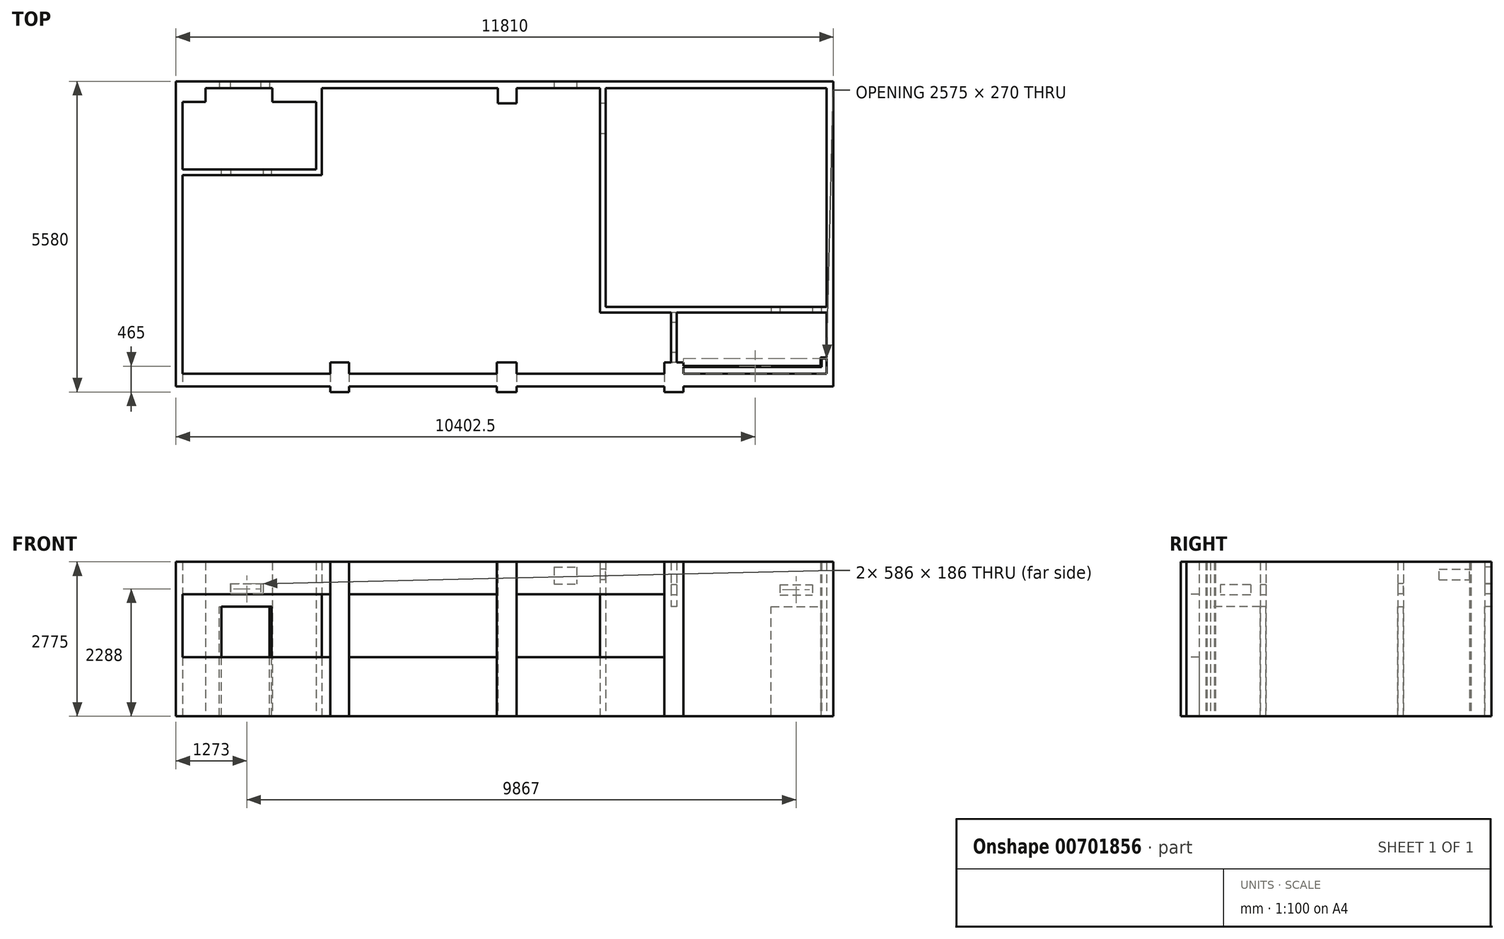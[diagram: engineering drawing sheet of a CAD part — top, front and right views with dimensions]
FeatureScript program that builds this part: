
annotation { "Feature Type Name" : "Feature", "Feature Type Description" : "" }
export const myFeature = defineFeature(function(context is Context, id is Id, definition is map)
    precondition{}
    {
        {
            var Q0;
            Q0=qCreatedBy(makeId("Top.planeOp"),FACE);
            var sketch = newSketch(context, id + "F0", { "sketchPlane" : qUnion([Q0])});
            skLineSegment(sketch, "E0.bottom", {"start": v(0, 0) * mm, "end": v(-5570, 0) * mm});
            skLineSegment(sketch, "E0.top", {"start": v(0, -5240) * mm, "end": v(-2575, -5240) * mm, "construction": true});
            skLineSegment(sketch, "E0.left", {"start": v(0, 0) * mm, "end": v(0, -5240) * mm});
            skLineSegment(sketch, "E0.right", {"start": v(-11570, -250) * mm, "end": v(-11570, -5130) * mm});
            skLineSegment(sketch, "E1.bottom", {"start": v(-11690, 120) * mm, "end": v(120, 120) * mm});
            skLineSegment(sketch, "E1.top", {"start": v(-11690, -5360) * mm, "end": v(-8920, -5360) * mm});
            skLineSegment(sketch, "E1.left", {"start": v(-11690, 120) * mm, "end": v(-11690, -5360) * mm});
            skLineSegment(sketch, "E1.right", {"start": v(120, 120) * mm, "end": v(120, -5360) * mm});
            skLineSegment(sketch, "E2.trimOffspring", {"start": v(-5925, -5240) * mm, "end": v(-8580, -5240) * mm, "construction": true});
            skLineSegment(sketch, "E3.trimOffspring", {"start": v(-5910, 0) * mm, "end": v(-9070, 0) * mm});
            skLineSegment(sketch, "E4", {"start": v(-5910, 0) * mm, "end": v(-5910, -275) * mm});
            skLineSegment(sketch, "E5", {"start": v(-5910, -275) * mm, "end": v(-5570, -275) * mm});
            skLineSegment(sketch, "E6", {"start": v(-5570, -275) * mm, "end": v(-5570, 0) * mm});
            skLineSegment(sketch, "E7", {"start": v(-5925, -5130) * mm, "end": v(-5925, -4930) * mm});
            skLineSegment(sketch, "E8", {"start": v(-5925, -4930) * mm, "end": v(-5570, -4930) * mm});
            skLineSegment(sketch, "E9", {"start": v(-5570, -4930) * mm, "end": v(-5570, -5130) * mm});
            skLineSegment(sketch, "E10.top", {"start": v(-8580, -4930) * mm, "end": v(-8920, -4930) * mm});
            skLineSegment(sketch, "E10.left", {"start": v(-8580, -5130) * mm, "end": v(-8580, -4930) * mm});
            skLineSegment(sketch, "E10.right", {"start": v(-8920, -5130) * mm, "end": v(-8920, -4930) * mm});
            skLineSegment(sketch, "E11.trimOffspring", {"start": v(-8920, -5240) * mm, "end": v(-11570, -5240) * mm, "construction": true});
            skLineSegment(sketch, "E12.top", {"start": v(-11570, -250) * mm, "end": v(-11160, -250) * mm});
            skLineSegment(sketch, "E12.right", {"start": v(-11160, 0) * mm, "end": v(-11160, -250) * mm});
            skLineSegment(sketch, "E13.top", {"start": v(-9960, -250) * mm, "end": v(-9070, -250) * mm});
            skLineSegment(sketch, "E13.left", {"start": v(-9960, 0) * mm, "end": v(-9960, -250) * mm});
            skLineSegment(sketch, "E13.right", {"start": v(-9070, 0) * mm, "end": v(-9070, -250) * mm});
            skLineSegment(sketch, "E14.trimOffspring", {"start": v(-9960, 0) * mm, "end": v(-11160, 0) * mm});
            skLineSegment(sketch, "E15.top", {"start": v(-2915, -4930) * mm, "end": v(-2575, -4930) * mm});
            skLineSegment(sketch, "E15.left", {"start": v(-2915, -5130) * mm, "end": v(-2915, -4930) * mm});
            skLineSegment(sketch, "E15.right", {"start": v(-2575, -5130) * mm, "end": v(-2575, -4930) * mm});
            skLineSegment(sketch, "E16.top", {"start": v(-2575, -5460) * mm, "end": v(-2915, -5460) * mm});
            skLineSegment(sketch, "E16.left", {"start": v(-2575, -5360) * mm, "end": v(-2575, -5460) * mm});
            skLineSegment(sketch, "E16.right", {"start": v(-2915, -5360) * mm, "end": v(-2915, -5460) * mm});
            skLineSegment(sketch, "E17.trimOffspring", {"start": v(-2575, -5360) * mm, "end": v(120, -5360) * mm});
            skLineSegment(sketch, "E18.trimOffspring", {"start": v(-2915, -5240) * mm, "end": v(-5570, -5240) * mm, "construction": true});
            skLineSegment(sketch, "E19.top", {"start": v(-5570, -5460) * mm, "end": v(-5925, -5460) * mm});
            skLineSegment(sketch, "E19.left", {"start": v(-5570, -5360) * mm, "end": v(-5570, -5460) * mm});
            skLineSegment(sketch, "E19.right", {"start": v(-5925, -5360) * mm, "end": v(-5925, -5460) * mm});
            skLineSegment(sketch, "E20.top", {"start": v(-8580, -5460) * mm, "end": v(-8920, -5460) * mm});
            skLineSegment(sketch, "E20.left", {"start": v(-8580, -5360) * mm, "end": v(-8580, -5460) * mm});
            skLineSegment(sketch, "E20.right", {"start": v(-8920, -5360) * mm, "end": v(-8920, -5460) * mm});
            skLineSegment(sketch, "E21.trimOffspring", {"start": v(-8580, -5360) * mm, "end": v(-5925, -5360) * mm});
            skLineSegment(sketch, "E22.trimOffspring", {"start": v(-5570, -5360) * mm, "end": v(-2915, -5360) * mm});
            skLineSegment(sketch, "E23", {"start": v(-11570, -5130) * mm, "end": v(-8920, -5130) * mm});
            skLineSegment(sketch, "E24.trimOffspring", {"start": v(-8580, -5130) * mm, "end": v(-5925, -5130) * mm});
            skLineSegment(sketch, "E25.trimOffspring", {"start": v(-5570, -5130) * mm, "end": v(-2915, -5130) * mm});
            skLineSegment(sketch, "E26.trimOffspring", {"start": v(-2575, -5130) * mm, "end": v(0, -5130) * mm});
            skSolve(sketch);
        }
        {
            var Q0;
            Q0=qSketchRegion(id+"F0",true);
            extrude(context, id + "F1", {"entities" : qUnion([Q0]), "depth" : 2775 * mm, "offsetDistance" : 25 * mm});
        }
        {
            var Q0;
            Q0=makeQuery(id+"F1.opExtrude","SWEPT_FACE",FACE,{"disambiguationData":[OSD([sQuery(id+"F0.wireOp",EDGE,"E0.bottom")])]});
            var sketch = newSketch(context, id + "F2", { "sketchPlane" : qUnion([Q0])});
            skLineSegment(sketch, "E27.bottom", {"start": v(-10910, 0) * mm, "end": v(-10010, 0) * mm});
            skLineSegment(sketch, "E27.top", {"start": v(-10910, 1970) * mm, "end": v(-10010, 1970) * mm});
            skLineSegment(sketch, "E27.left", {"start": v(-10910, 0) * mm, "end": v(-10910, 1970) * mm});
            skLineSegment(sketch, "E27.right", {"start": v(-10010, 0) * mm, "end": v(-10010, 1970) * mm});
            skSolve(sketch);
        }
        {
            var Q0;
            Q0=qSketchRegion(id+"F2",true);
            extrude(context, id + "F3", {"entities" : qUnion([Q0]), "operationType" : NewBodyOperationType.REMOVE, "endBound" : BoundingType.UP_TO_NEXT, "oppositeDirection" : true, "depth" : 25 * mm, "offsetDistance" : 25 * mm});
        }
        {
            var Q0;
            Q0=qCreatedBy(makeId("Top.planeOp"),FACE);
            var sketch = newSketch(context, id + "F4", { "sketchPlane" : qUnion([Q0])});
            skLineSegment(sketch, "E28.bottom", {"start": v(-9070, -1460) * mm, "end": v(-11570, -1460) * mm});
            skLineSegment(sketch, "E28.top", {"start": v(-9070, -1560) * mm, "end": v(-11570, -1560) * mm});
            skLineSegment(sketch, "E28.right", {"start": v(-11570, -1460) * mm, "end": v(-11570, -1560) * mm});
            skLineSegment(sketch, "E29", {"start": v(-9070, -1460) * mm, "end": v(-9070, -1560) * mm});
            skSolve(sketch);
        }
        {
            var Q0;
            Q0=makeQuery(id+"F4.imprint","IMPRINT",FACE,{"disambiguationData":[TD([[makeQuery(id+"F4.imprint","IMPRINT",EDGE,{"derivedFrom":sQuery(id+"F4.wireOp",EDGE,"E28.bottom")}),1.0]])]});
            var Q1;
            {var subQ0=sQuery(id+"F0.wireOp",EDGE,"E1.right");var subQ1=sQuery(id+"F0.wireOp",EDGE,"E1.left");var subQ2=sQuery(id+"F0.wireOp",EDGE,"E1.top");var subQ3=sQuery(id+"F0.wireOp",EDGE,"E1.bottom");var subQ4=sQuery(id+"F0.wireOp",EDGE,"E0.right");var subQ5=sQuery(id+"F0.wireOp",EDGE,"E0.left");var subQ6=sQuery(id+"F0.wireOp",EDGE,"E0.top");var subQ7=sQuery(id+"F0.wireOp",EDGE,"E0.bottom");Q1=makeQuery(id+"FWLc4urFRa7aNsW_1.boolean.opBoolean","MERGE",FACE,{"derivedFrom":[makeQuery(id+"F1.opExtrude","CAP_FACE",FACE,{"disambiguationData":[OSD([subQ7,subQ6,subQ5,subQ4,subQ3,subQ2,subQ1,subQ0])],"isStart":false}),makeQuery(id+"FWLc4urFRa7aNsW_1.opExtrude","CAP_FACE",FACE,{"disambiguationData":[OSD([subQ7,subQ6,subQ5,subQ4,subQ3,subQ2,subQ1,subQ0])],"isStart":false})]});}
            extrude(context, id + "F5", {"entities" : qUnion([Q0]), "operationType" : NewBodyOperationType.ADD, "endBound" : BoundingType.UP_TO_SURFACE, "depth" : 25 * mm, "endBoundEntityFace" : qUnion([Q1]), "offsetDistance" : 25 * mm});
        }
        {
            var Q0;
            Q0=qCreatedBy(makeId("Top.planeOp"),FACE);
            var sketch = newSketch(context, id + "F6", { "sketchPlane" : qUnion([Q0])});
            skLineSegment(sketch, "E30.bottom", {"start": v(-9070, 0) * mm, "end": v(-9170, 0) * mm});
            skLineSegment(sketch, "E30.top", {"start": v(-9070, -1460) * mm, "end": v(-9170, -1460) * mm});
            skLineSegment(sketch, "E30.left", {"start": v(-9070, 0) * mm, "end": v(-9070, -1460) * mm});
            skLineSegment(sketch, "E30.right", {"start": v(-9170, 0) * mm, "end": v(-9170, -1460) * mm});
            skSolve(sketch);
        }
        {
            var Q0;
            Q0=makeQuery(id+"F6.imprint","IMPRINT",FACE,{"disambiguationData":[TD([[makeQuery(id+"F6.imprint","IMPRINT",EDGE,{"derivedFrom":sQuery(id+"F6.wireOp",EDGE,"E30.bottom")}),1.0]])]});
            var Q1;
            {var subQ0=sQuery(id+"F0.wireOp",EDGE,"E1.right");var subQ1=sQuery(id+"F0.wireOp",EDGE,"E1.left");var subQ2=sQuery(id+"F0.wireOp",EDGE,"E1.top");var subQ3=sQuery(id+"F0.wireOp",EDGE,"E1.bottom");var subQ4=sQuery(id+"F0.wireOp",EDGE,"E0.right");var subQ5=sQuery(id+"F0.wireOp",EDGE,"E0.left");var subQ6=sQuery(id+"F0.wireOp",EDGE,"E0.top");var subQ7=sQuery(id+"F0.wireOp",EDGE,"E0.bottom");Q1=makeQuery(id+"F5.boolean.opBoolean","MERGE",FACE,{"derivedFrom":[makeQuery(id+"FWLc4urFRa7aNsW_1.boolean.opBoolean","MERGE",FACE,{"derivedFrom":[makeQuery(id+"F1.opExtrude","CAP_FACE",FACE,{"disambiguationData":[OSD([subQ7,subQ6,subQ5,subQ4,subQ3,subQ2,subQ1,subQ0])],"isStart":false}),makeQuery(id+"FWLc4urFRa7aNsW_1.opExtrude","CAP_FACE",FACE,{"disambiguationData":[OSD([subQ7,subQ6,subQ5,subQ4,subQ3,subQ2,subQ1,subQ0])],"isStart":false})]}),makeQuery(id+"F5.opExtrude","CAP_FACE",FACE,{"disambiguationData":[OSD([subQ7,subQ6,subQ5,subQ4,subQ3,subQ2,subQ1,subQ0])],"isStart":false})]});}
            extrude(context, id + "F7", {"entities" : qUnion([Q0]), "operationType" : NewBodyOperationType.ADD, "endBound" : BoundingType.UP_TO_SURFACE, "depth" : 25 * mm, "endBoundEntityFace" : qUnion([Q1]), "offsetDistance" : 25 * mm});
        }
        {
            var Q0;
            {var subQ0=sQuery(id+"F0.wireOp",EDGE,"E0.right");var subQ8=sQuery(id+"F4.wireOp",EDGE,"E28.bottom");Q0=makeQuery(id+"F7.boolean.opBoolean","SPLIT",FACE,{"disambiguationData":[TD([makeQuery(id+"F1.opExtrude","SWEPT_FACE",FACE,{"disambiguationData":[OSD([subQ0])]})])],"derivedFrom":makeQuery(id+"F5.opExtrude","SWEPT_FACE",FACE,{"disambiguationData":[OSD([subQ8])]})});}
            var sketch = newSketch(context, id + "F8", { "sketchPlane" : qUnion([Q0])});
            skLineSegment(sketch, "E31.bottom", {"start": v(9970, 0) * mm, "end": v(10870, 0) * mm});
            skLineSegment(sketch, "E31.top", {"start": v(9970, 1970) * mm, "end": v(10870, 1970) * mm});
            skLineSegment(sketch, "E31.left", {"start": v(9970, 0) * mm, "end": v(9970, 1970) * mm});
            skLineSegment(sketch, "E31.right", {"start": v(10870, 0) * mm, "end": v(10870, 1970) * mm});
            skSolve(sketch);
        }
        {
            var Q0;
            Q0=makeQuery(id+"F8.imprint","IMPRINT",FACE,{"disambiguationData":[TD([[makeQuery(id+"F8.imprint","IMPRINT",EDGE,{"derivedFrom":sQuery(id+"F8.wireOp",EDGE,"E31.bottom")}),1.0]])]});
            extrude(context, id + "F9", {"entities" : qUnion([Q0]), "operationType" : NewBodyOperationType.REMOVE, "endBound" : BoundingType.UP_TO_NEXT, "oppositeDirection" : true, "depth" : 25 * mm, "offsetDistance" : 25 * mm});
        }
        {
            var Q0;
            Q0=qCreatedBy(makeId("Top.planeOp"),FACE);
            var sketch = newSketch(context, id + "F10", { "sketchPlane" : qUnion([Q0])});
            skLineSegment(sketch, "E32", {"start": v(-3970, -3930) * mm, "end": v(0, -3930) * mm});
            skLineSegment(sketch, "E33", {"start": v(-3970, -3930) * mm, "end": v(-3970, 0) * mm});
            skLineSegment(sketch, "E34", {"start": v(-3970, 0) * mm, "end": v(-4070, 0) * mm});
            skLineSegment(sketch, "E35", {"start": v(-4070, 0) * mm, "end": v(-4070, -4030) * mm});
            skLineSegment(sketch, "E36", {"start": v(-2795, -4030) * mm, "end": v(-4070, -4030) * mm});
            skLineSegment(sketch, "E37", {"start": v(0, -3930) * mm, "end": v(0, -4030) * mm});
            skLineSegment(sketch, "E38.top", {"start": v(-2795, -4930) * mm, "end": v(-2695, -4930) * mm});
            skLineSegment(sketch, "E38.left", {"start": v(-2795, -4030) * mm, "end": v(-2795, -4930) * mm});
            skLineSegment(sketch, "E38.right", {"start": v(-2695, -4030) * mm, "end": v(-2695, -4930) * mm});
            skPoint(sketch, "E39", {"position": v(-2745, -4930) * mm});
            skLineSegment(sketch, "E40.trimOffspring", {"start": v(0, -4030) * mm, "end": v(-2695, -4030) * mm});
            skSolve(sketch);
        }
        {
            var Q0;
            Q0=makeQuery(id+"F10.imprint","IMPRINT",FACE,{"disambiguationData":[TD([[makeQuery(id+"F10.imprint","IMPRINT",EDGE,{"derivedFrom":sQuery(id+"F10.wireOp",EDGE,"E32")}),-1.0]])]});
            extrude(context, id + "F11", {"entities" : qUnion([Q0]), "operationType" : NewBodyOperationType.ADD, "depth" : 2775 * mm, "offsetDistance" : 25 * mm});
        }
        {
            var Q0;
            Q0=makeQuery(id+"F1.opExtrude","SWEPT_FACE",FACE,{"disambiguationData":[OSD([sQuery(id+"F0.wireOp",EDGE,"E1.top")])]});
            var sketch = newSketch(context, id + "F12", { "sketchPlane" : qUnion([Q0])});
            skLineSegment(sketch, "E41.bottom", {"start": v(-2915, 2190) * mm, "end": v(-5570, 2190) * mm});
            skLineSegment(sketch, "E41.top", {"start": v(-2915, 1060) * mm, "end": v(-5570, 1060) * mm});
            skLineSegment(sketch, "E41.left", {"start": v(-2915, 2190) * mm, "end": v(-2915, 1060) * mm});
            skLineSegment(sketch, "E41.right", {"start": v(-5570, 2190) * mm, "end": v(-5570, 1060) * mm});
            skSolve(sketch);
        }
        {
            var Q0;
            Q0=makeQuery(id+"F12.imprint","IMPRINT",FACE,{"disambiguationData":[TD([[makeQuery(id+"F12.imprint","IMPRINT",EDGE,{"derivedFrom":sQuery(id+"F12.wireOp",EDGE,"UQFrSV9A-AeNk-hTGs-XUq7-kkI5QUDZIYbv.bottom")}),1.0]])]});
            var Q1;
            Q1=makeQuery(id+"F12.imprint","IMPRINT",FACE,{"disambiguationData":[TD([[makeQuery(id+"F12.imprint","IMPRINT",EDGE,{"derivedFrom":sQuery(id+"F12.wireOp",EDGE,"E41.bottom")}),1.0]])]});
            extrude(context, id + "F13", {"entities" : qUnion([Q0, Q1]), "operationType" : NewBodyOperationType.REMOVE, "endBound" : BoundingType.UP_TO_NEXT, "oppositeDirection" : true, "depth" : 25 * mm, "offsetDistance" : 25 * mm});
        }
        {
            var Q0;
            Q0=makeQuery(id+"F1.opExtrude","SWEPT_FACE",FACE,{"disambiguationData":[OSD([sQuery(id+"F0.wireOp",EDGE,"E1.top")])]});
            var sketch = newSketch(context, id + "F14", { "sketchPlane" : qUnion([Q0])});
            skLineSegment(sketch, "E42.bottom", {"start": v(-5925, 2190) * mm, "end": v(-8580, 2190) * mm});
            skLineSegment(sketch, "E42.top", {"start": v(-5925, 1060) * mm, "end": v(-8580, 1060) * mm});
            skLineSegment(sketch, "E42.left", {"start": v(-5925, 2190) * mm, "end": v(-5925, 1060) * mm});
            skLineSegment(sketch, "E42.right", {"start": v(-8580, 2190) * mm, "end": v(-8580, 1060) * mm});
            skLineSegment(sketch, "E43.bottom", {"start": v(-8920, 2190) * mm, "end": v(-11570, 2190) * mm});
            skLineSegment(sketch, "E43.top", {"start": v(-8920, 1060) * mm, "end": v(-11570, 1060) * mm});
            skLineSegment(sketch, "E43.left", {"start": v(-8920, 2190) * mm, "end": v(-8920, 1060) * mm});
            skLineSegment(sketch, "E43.right", {"start": v(-11570, 2190) * mm, "end": v(-11570, 1060) * mm});
            skSolve(sketch);
        }
        {
            var Q0;
            Q0=makeQuery(id+"F14.imprint","IMPRINT",FACE,{"disambiguationData":[TD([[makeQuery(id+"F14.imprint","IMPRINT",EDGE,{"derivedFrom":sQuery(id+"F14.wireOp",EDGE,"E43.bottom")}),1.0]])]});
            var Q1;
            Q1=makeQuery(id+"F14.imprint","IMPRINT",FACE,{"disambiguationData":[TD([[makeQuery(id+"F14.imprint","IMPRINT",EDGE,{"derivedFrom":sQuery(id+"F14.wireOp",EDGE,"E42.bottom")}),1.0]])]});
            extrude(context, id + "F15", {"entities" : qUnion([Q0, Q1]), "operationType" : NewBodyOperationType.REMOVE, "endBound" : BoundingType.UP_TO_NEXT, "oppositeDirection" : true, "depth" : 25 * mm, "offsetDistance" : 25 * mm});
        }
        {
            var Q0;
            Q0=makeQuery(id+"F1.opExtrude","SWEPT_FACE",FACE,{"disambiguationData":[OSD([sQuery(id+"F0.wireOp",EDGE,"E3.trimOffspring")])]});
            var sketch = newSketch(context, id + "F16", { "sketchPlane" : qUnion([Q0])});
            skLineSegment(sketch, "E44.bottom", {"start": v(-4896, 2680) * mm, "end": v(-4490, 2680) * mm});
            skLineSegment(sketch, "E44.top", {"start": v(-4896, 2374) * mm, "end": v(-4490, 2374) * mm});
            skLineSegment(sketch, "E44.left", {"start": v(-4896, 2680) * mm, "end": v(-4896, 2374) * mm});
            skLineSegment(sketch, "E44.right", {"start": v(-4490, 2680) * mm, "end": v(-4490, 2374) * mm});
            skSolve(sketch);
        }
        {
            var Q0;
            Q0=makeQuery(id+"F16.imprint","IMPRINT",FACE,{"disambiguationData":[TD([[makeQuery(id+"F16.imprint","IMPRINT",EDGE,{"derivedFrom":sQuery(id+"F16.wireOp",EDGE,"E44.bottom")}),-1.0]])]});
            extrude(context, id + "F17", {"entities" : qUnion([Q0]), "operationType" : NewBodyOperationType.REMOVE, "endBound" : BoundingType.UP_TO_NEXT, "oppositeDirection" : true, "depth" : 25 * mm, "offsetDistance" : 25 * mm});
        }
        {
            var Q0;
            Q0=makeQuery(id+"F11.opExtrude","SWEPT_FACE",FACE,{"disambiguationData":[OSD([sQuery(id+"F10.wireOp",EDGE,"E35")])]});
            var sketch = newSketch(context, id + "F18", { "sketchPlane" : qUnion([Q0])});
            skLineSegment(sketch, "E45.bottom", {"start": v(275, 2640) * mm, "end": v(821, 2640) * mm});
            skLineSegment(sketch, "E45.top", {"start": v(275, 2454) * mm, "end": v(821, 2454) * mm});
            skLineSegment(sketch, "E45.left", {"start": v(275, 2640) * mm, "end": v(275, 2454) * mm});
            skLineSegment(sketch, "E45.right", {"start": v(821, 2640) * mm, "end": v(821, 2454) * mm});
            skSolve(sketch);
        }
        {
            var Q0;
            Q0=makeQuery(id+"F18.imprint","IMPRINT",FACE,{"disambiguationData":[TD([[makeQuery(id+"F18.imprint","IMPRINT",EDGE,{"derivedFrom":sQuery(id+"F18.wireOp",EDGE,"E45.bottom")}),-1.0]])]});
            extrude(context, id + "F19", {"entities" : qUnion([Q0]), "operationType" : NewBodyOperationType.REMOVE, "endBound" : BoundingType.UP_TO_NEXT, "oppositeDirection" : true, "depth" : 25 * mm, "offsetDistance" : 25 * mm});
        }
        {
            var Q0;
            Q0=makeQuery(id+"F1.opExtrude","SWEPT_FACE",FACE,{"disambiguationData":[OSD([sQuery(id+"F0.wireOp",EDGE,"E14.trimOffspring")])]});
            var sketch = newSketch(context, id + "F20", { "sketchPlane" : qUnion([Q0])});
            skLineSegment(sketch, "E46.bottom", {"start": v(-10716, 2381) * mm, "end": v(-10170, 2381) * mm});
            skLineSegment(sketch, "E46.top", {"start": v(-10716, 2195) * mm, "end": v(-10170, 2195) * mm});
            skLineSegment(sketch, "E46.left", {"start": v(-10716, 2381) * mm, "end": v(-10716, 2195) * mm});
            skLineSegment(sketch, "E46.right", {"start": v(-10170, 2381) * mm, "end": v(-10170, 2195) * mm});
            skSolve(sketch);
        }
        {
            var Q0;
            Q0=makeQuery(id+"F20.imprint","IMPRINT",FACE,{"disambiguationData":[TD([[makeQuery(id+"F20.imprint","IMPRINT",EDGE,{"derivedFrom":sQuery(id+"F20.wireOp",EDGE,"E46.bottom")}),-1.0]])]});
            extrude(context, id + "F21", {"entities" : qUnion([Q0]), "operationType" : NewBodyOperationType.REMOVE, "endBound" : BoundingType.UP_TO_NEXT, "oppositeDirection" : true, "depth" : 25 * mm, "offsetDistance" : 25 * mm});
        }
        {
            var Q0;
            Q0=makeQuery(id+"F5.opExtrude","SWEPT_FACE",FACE,{"disambiguationData":[OSD([sQuery(id+"F4.wireOp",EDGE,"E28.top")])]});
            var sketch = newSketch(context, id + "F22", { "sketchPlane" : qUnion([Q0])});
            skLineSegment(sketch, "E47.bottom", {"start": v(-10710, 2381) * mm, "end": v(-10124, 2381) * mm});
            skLineSegment(sketch, "E47.top", {"start": v(-10710, 2195) * mm, "end": v(-10124, 2195) * mm});
            skLineSegment(sketch, "E47.left", {"start": v(-10710, 2381) * mm, "end": v(-10710, 2195) * mm});
            skLineSegment(sketch, "E47.right", {"start": v(-10124, 2381) * mm, "end": v(-10124, 2195) * mm});
            skSolve(sketch);
        }
        {
            var Q0;
            Q0=makeQuery(id+"F22.imprint","IMPRINT",FACE,{"disambiguationData":[TD([[makeQuery(id+"F22.imprint","IMPRINT",EDGE,{"derivedFrom":sQuery(id+"F22.wireOp",EDGE,"E47.bottom")}),-1.0]])]});
            extrude(context, id + "F23", {"entities" : qUnion([Q0]), "operationType" : NewBodyOperationType.REMOVE, "endBound" : BoundingType.UP_TO_NEXT, "oppositeDirection" : true, "depth" : 25 * mm, "offsetDistance" : 25 * mm});
        }
        {
            var Q0;
            Q0=qCreatedBy(makeId("Top.planeOp"),FACE);
            var sketch = newSketch(context, id + "F24", { "sketchPlane" : qUnion([Q0])});
            skLineSegment(sketch, "E48.bottom", {"start": v(-2575, -4990) * mm, "end": v(-110, -4990) * mm});
            skLineSegment(sketch, "E48.top", {"start": v(-2575, -5010) * mm, "end": v(-90, -5010) * mm});
            skLineSegment(sketch, "E48.left", {"start": v(-2575, -4990) * mm, "end": v(-2575, -5010) * mm});
            skLineSegment(sketch, "E49.bottom", {"start": v(0, -4840) * mm, "end": v(-110, -4840) * mm});
            skLineSegment(sketch, "E49.left", {"start": v(0, -4840) * mm, "end": v(0, -4860) * mm});
            skLineSegment(sketch, "E49.right", {"start": v(-110, -4840) * mm, "end": v(-110, -4990) * mm});
            skLineSegment(sketch, "E50.0", {"start": v(-90, -4860) * mm, "end": v(-90, -5010) * mm});
            skLineSegment(sketch, "E50.1", {"start": v(0, -4860) * mm, "end": v(-90, -4860) * mm});
            skSolve(sketch);
        }
        {
            var Q0;
            Q0=makeQuery(id+"F24.imprint","IMPRINT",FACE,{"disambiguationData":[TD([[makeQuery(id+"F24.imprint","IMPRINT",EDGE,{"derivedFrom":sQuery(id+"F24.wireOp",EDGE,"E48.bottom")}),-1.0]])]});
            var Q1;
            {var subQ0=sQuery(id+"F0.wireOp",EDGE,"E26.trimOffspring");var subQ1=sQuery(id+"F0.wireOp",EDGE,"E25.trimOffspring");var subQ2=sQuery(id+"F0.wireOp",EDGE,"E24.trimOffspring");var subQ3=sQuery(id+"F0.wireOp",EDGE,"E23");var subQ4=sQuery(id+"F0.wireOp",EDGE,"E22.trimOffspring");var subQ5=sQuery(id+"F0.wireOp",EDGE,"E21.trimOffspring");var subQ6=sQuery(id+"F0.wireOp",EDGE,"E20.right");var subQ7=sQuery(id+"F0.wireOp",EDGE,"E20.left");var subQ8=sQuery(id+"F0.wireOp",EDGE,"E20.top");var subQ9=sQuery(id+"F0.wireOp",EDGE,"E19.right");var subQ10=sQuery(id+"F0.wireOp",EDGE,"E19.left");var subQ11=sQuery(id+"F0.wireOp",EDGE,"E19.top");var subQ12=sQuery(id+"F0.wireOp",EDGE,"E17.trimOffspring");var subQ13=sQuery(id+"F0.wireOp",EDGE,"E16.right");var subQ14=sQuery(id+"F0.wireOp",EDGE,"E16.left");var subQ15=sQuery(id+"F0.wireOp",EDGE,"E16.top");var subQ16=sQuery(id+"F0.wireOp",EDGE,"E15.right");var subQ17=sQuery(id+"F0.wireOp",EDGE,"E15.left");var subQ18=sQuery(id+"F0.wireOp",EDGE,"E15.top");var subQ19=sQuery(id+"F0.wireOp",EDGE,"E14.trimOffspring");var subQ20=sQuery(id+"F0.wireOp",EDGE,"E13.right");var subQ21=sQuery(id+"F0.wireOp",EDGE,"E13.left");var subQ22=sQuery(id+"F0.wireOp",EDGE,"E13.top");var subQ23=sQuery(id+"F0.wireOp",EDGE,"E12.right");var subQ24=sQuery(id+"F0.wireOp",EDGE,"E12.top");var subQ25=sQuery(id+"F0.wireOp",EDGE,"E10.right");var subQ26=sQuery(id+"F0.wireOp",EDGE,"E10.left");var subQ27=sQuery(id+"F0.wireOp",EDGE,"E10.top");var subQ28=sQuery(id+"F0.wireOp",EDGE,"E9");var subQ29=sQuery(id+"F0.wireOp",EDGE,"E8");var subQ30=sQuery(id+"F0.wireOp",EDGE,"E7");var subQ31=sQuery(id+"F0.wireOp",EDGE,"E6");var subQ32=sQuery(id+"F0.wireOp",EDGE,"E5");var subQ33=sQuery(id+"F0.wireOp",EDGE,"E4");var subQ34=sQuery(id+"F0.wireOp",EDGE,"E3.trimOffspring");var subQ35=sQuery(id+"F0.wireOp",EDGE,"E1.right");var subQ36=sQuery(id+"F0.wireOp",EDGE,"E1.left");var subQ37=sQuery(id+"F0.wireOp",EDGE,"E1.top");var subQ38=sQuery(id+"F0.wireOp",EDGE,"E1.bottom");var subQ39=sQuery(id+"F0.wireOp",EDGE,"E0.right");var subQ40=sQuery(id+"F0.wireOp",EDGE,"E0.left");var subQ41=sQuery(id+"F0.wireOp",EDGE,"E0.bottom");Q1=makeQuery(id+"F11.boolean.opBoolean","MERGE",FACE,{"derivedFrom":[makeQuery(id+"F8GBdiIUWhZT2El_1.boolean.opBoolean","MERGE",FACE,{"derivedFrom":[makeQuery(id+"F7.boolean.opBoolean","MERGE",FACE,{"derivedFrom":[makeQuery(id+"F5.boolean.opBoolean","MERGE",FACE,{"derivedFrom":[makeQuery(id+"FWLc4urFRa7aNsW_1.boolean.opBoolean","MERGE",FACE,{"derivedFrom":[makeQuery(id+"F1.opExtrude","CAP_FACE",FACE,{"disambiguationData":[OSD([subQ41,subQ40,subQ39,subQ38,subQ37,subQ36,subQ35,subQ34,subQ33,subQ32,subQ31,subQ30,subQ29,subQ28,subQ27,subQ26,subQ25,subQ24,subQ23,subQ22,subQ21,subQ20,subQ19,subQ18,subQ17,subQ16,subQ15,subQ14,subQ13,subQ12,subQ11,subQ10,subQ9,subQ8,subQ7,subQ6,subQ5,subQ4,subQ3,subQ2,subQ1,subQ0])],"isStart":false}),makeQuery(id+"FWLc4urFRa7aNsW_1.opExtrude","CAP_FACE",FACE,{"disambiguationData":[OSD([subQ41,subQ40,subQ39,subQ38,subQ37,subQ36,subQ35,subQ34,subQ33,subQ32,subQ31,subQ30,subQ29,subQ28,subQ27,subQ26,subQ25,subQ24,subQ23,subQ22,subQ21,subQ20,subQ19,subQ18,subQ17,subQ16,subQ15,subQ14,subQ13,subQ12,subQ11,subQ10,subQ9,subQ8,subQ7,subQ6,subQ5,subQ4,subQ3,subQ2,subQ1,subQ0])],"isStart":false})]}),makeQuery(id+"F5.opExtrude","CAP_FACE",FACE,{"disambiguationData":[OSD([subQ41,subQ40,subQ39,subQ38,subQ37,subQ36,subQ35,subQ34,subQ33,subQ32,subQ31,subQ30,subQ29,subQ28,subQ27,subQ26,subQ25,subQ24,subQ23,subQ22,subQ21,subQ20,subQ19,subQ18,subQ17,subQ16,subQ15,subQ14,subQ13,subQ12,subQ11,subQ10,subQ9,subQ8,subQ7,subQ6,subQ5,subQ4,subQ3,subQ2,subQ1,subQ0])],"isStart":false})]}),makeQuery(id+"F7.opExtrude","CAP_FACE",FACE,{"disambiguationData":[OSD([subQ41,subQ40,subQ39,subQ38,subQ37,subQ36,subQ35,subQ34,subQ33,subQ32,subQ31,subQ30,subQ29,subQ28,subQ27,subQ26,subQ25,subQ24,subQ23,subQ22,subQ21,subQ20,subQ19,subQ18,subQ17,subQ16,subQ15,subQ14,subQ13,subQ12,subQ11,subQ10,subQ9,subQ8,subQ7,subQ6,subQ5,subQ4,subQ3,subQ2,subQ1,subQ0])],"isStart":false})]}),makeQuery(id+"F8GBdiIUWhZT2El_1.opExtrude","CAP_FACE",FACE,{"disambiguationData":[OSD([subQ41,subQ40,subQ39,subQ38,subQ37,subQ36,subQ35,subQ34,subQ33,subQ32,subQ31,subQ30,subQ29,subQ28,subQ27,subQ26,subQ25,subQ24,subQ23,subQ22,subQ21,subQ20,subQ19,subQ18,subQ17,subQ16,subQ15,subQ14,subQ13,subQ12,subQ11,subQ10,subQ9,subQ8,subQ7,subQ6,subQ5,subQ4,subQ3,subQ2,subQ1,subQ0])],"isStart":false})]}),makeQuery(id+"F11.opExtrude","CAP_FACE",FACE,{"disambiguationData":[OSD([subQ41,subQ40,subQ39,subQ38,subQ37,subQ36,subQ35,subQ34,subQ33,subQ32,subQ31,subQ30,subQ29,subQ28,subQ27,subQ26,subQ25,subQ24,subQ23,subQ22,subQ21,subQ20,subQ19,subQ18,subQ17,subQ16,subQ15,subQ14,subQ13,subQ12,subQ11,subQ10,subQ9,subQ8,subQ7,subQ6,subQ5,subQ4,subQ3,subQ2,subQ1,subQ0])],"isStart":false})]});}
            extrude(context, id + "F25", {"entities" : qUnion([Q0]), "operationType" : NewBodyOperationType.ADD, "endBound" : BoundingType.UP_TO_SURFACE, "depth" : 25 * mm, "endBoundEntityFace" : qUnion([Q1]), "offsetDistance" : 25 * mm});
        }
        {
            var Q0;
            Q0=makeQuery(id+"F11.opExtrude","SWEPT_FACE",FACE,{"disambiguationData":[OSD([sQuery(id+"F10.wireOp",EDGE,"E38.left")])]});
            var sketch = newSketch(context, id + "F26", { "sketchPlane" : qUnion([Q0])});
            skLineSegment(sketch, "E51.bottom", {"start": v(4030, 0) * mm, "end": v(4930, 0) * mm});
            skLineSegment(sketch, "E51.top", {"start": v(4030, 1970) * mm, "end": v(4930, 1970) * mm});
            skLineSegment(sketch, "E51.left", {"start": v(4030, 0) * mm, "end": v(4030, 1970) * mm});
            skLineSegment(sketch, "E51.right", {"start": v(4930, 0) * mm, "end": v(4930, 1970) * mm});
            skSolve(sketch);
        }
        {
            var Q0;
            Q0=makeQuery(id+"F26.imprint","IMPRINT",FACE,{"disambiguationData":[TD([[makeQuery(id+"F26.imprint","IMPRINT",EDGE,{"derivedFrom":sQuery(id+"F26.wireOp",EDGE,"E51.bottom")}),1.0]])]});
            extrude(context, id + "F27", {"entities" : qUnion([Q0]), "operationType" : NewBodyOperationType.REMOVE, "endBound" : BoundingType.UP_TO_NEXT, "oppositeDirection" : true, "depth" : 25 * mm, "offsetDistance" : 25 * mm});
        }
        {
            var Q0;
            Q0=makeQuery(id+"F11.opExtrude","SWEPT_FACE",FACE,{"disambiguationData":[OSD([sQuery(id+"F10.wireOp",EDGE,"E38.left")])]});
            var sketch = newSketch(context, id + "F28", { "sketchPlane" : qUnion([Q0])});
            skLineSegment(sketch, "E52.bottom", {"start": v(4207, 2366) * mm, "end": v(4753, 2366) * mm});
            skLineSegment(sketch, "E52.top", {"start": v(4207, 2180) * mm, "end": v(4753, 2180) * mm});
            skLineSegment(sketch, "E52.left", {"start": v(4207, 2366) * mm, "end": v(4207, 2180) * mm});
            skLineSegment(sketch, "E52.right", {"start": v(4753, 2366) * mm, "end": v(4753, 2180) * mm});
            skPoint(sketch, "E53", {"position": v(4480, 2180) * mm});
            skSolve(sketch);
        }
        {
            var Q0;
            Q0=makeQuery(id+"F28.imprint","IMPRINT",FACE,{"disambiguationData":[TD([[makeQuery(id+"F28.imprint","IMPRINT",EDGE,{"derivedFrom":sQuery(id+"F28.wireOp",EDGE,"E52.bottom")}),-1.0]])]});
            extrude(context, id + "F29", {"entities" : qUnion([Q0]), "operationType" : NewBodyOperationType.REMOVE, "endBound" : BoundingType.UP_TO_NEXT, "oppositeDirection" : true, "depth" : 25 * mm, "offsetDistance" : 25 * mm});
        }
        {
            var Q0;
            Q0=makeQuery(id+"F27.boolean.opBoolean","MERGE",FACE,{"derivedFrom":[makeQuery(id+"F11.opExtrude","SWEPT_FACE",FACE,{"disambiguationData":[OSD([sQuery(id+"F10.wireOp",EDGE,"E36")])]}),makeQuery(id+"F11.opExtrude","SWEPT_FACE",FACE,{"disambiguationData":[OSD([sQuery(id+"F10.wireOp",EDGE,"E40.trimOffspring")])]}),makeQuery(id+"F27.opExtrude","SWEPT_FACE",FACE,{"disambiguationData":[OSD([sQuery(id+"F26.wireOp",EDGE,"E51.left")])]})]});
            var sketch = newSketch(context, id + "F30", { "sketchPlane" : qUnion([Q0])});
            skLineSegment(sketch, "E54.bottom", {"start": v(-1000, 0) * mm, "end": v(-100, 0) * mm});
            skLineSegment(sketch, "E54.top", {"start": v(-1000, 1970) * mm, "end": v(-100, 1970) * mm});
            skLineSegment(sketch, "E54.left", {"start": v(-1000, 0) * mm, "end": v(-1000, 1970) * mm});
            skLineSegment(sketch, "E54.right", {"start": v(-100, 0) * mm, "end": v(-100, 1970) * mm});
            skSolve(sketch);
        }
        {
            var Q0;
            Q0=makeQuery(id+"F30.imprint","IMPRINT",FACE,{"disambiguationData":[TD([[makeQuery(id+"F30.imprint","IMPRINT",EDGE,{"derivedFrom":sQuery(id+"F30.wireOp",EDGE,"E54.bottom")}),-1.0]])]});
            extrude(context, id + "F31", {"entities" : qUnion([Q0]), "operationType" : NewBodyOperationType.REMOVE, "endBound" : BoundingType.UP_TO_NEXT, "oppositeDirection" : true, "depth" : 25 * mm, "offsetDistance" : 25 * mm});
        }
        {
            var Q0;
            Q0=makeQuery(id+"F27.boolean.opBoolean","MERGE",FACE,{"derivedFrom":[makeQuery(id+"F11.opExtrude","SWEPT_FACE",FACE,{"disambiguationData":[OSD([sQuery(id+"F10.wireOp",EDGE,"E36")])]}),makeQuery(id+"F11.opExtrude","SWEPT_FACE",FACE,{"disambiguationData":[OSD([sQuery(id+"F10.wireOp",EDGE,"E40.trimOffspring")])]}),makeQuery(id+"F27.opExtrude","SWEPT_FACE",FACE,{"disambiguationData":[OSD([sQuery(id+"F26.wireOp",EDGE,"E51.left")])]})]});
            var sketch = newSketch(context, id + "F32", { "sketchPlane" : qUnion([Q0])});
            skLineSegment(sketch, "E55.bottom", {"start": v(-843, 2366) * mm, "end": v(-257, 2366) * mm});
            skLineSegment(sketch, "E55.top", {"start": v(-843, 2180) * mm, "end": v(-257, 2180) * mm});
            skLineSegment(sketch, "E55.left", {"start": v(-843, 2366) * mm, "end": v(-843, 2180) * mm});
            skLineSegment(sketch, "E55.right", {"start": v(-257, 2366) * mm, "end": v(-257, 2180) * mm});
            skPoint(sketch, "E56", {"position": v(-550, 2180) * mm});
            skSolve(sketch);
        }
        {
            var Q0;
            Q0=makeQuery(id+"F32.imprint","IMPRINT",FACE,{"disambiguationData":[TD([[makeQuery(id+"F32.imprint","IMPRINT",EDGE,{"derivedFrom":sQuery(id+"F32.wireOp",EDGE,"E55.bottom")}),-1.0]])]});
            extrude(context, id + "F33", {"entities" : qUnion([Q0]), "operationType" : NewBodyOperationType.REMOVE, "endBound" : BoundingType.UP_TO_NEXT, "oppositeDirection" : true, "depth" : 25 * mm, "offsetDistance" : 25 * mm});
        }
    });
